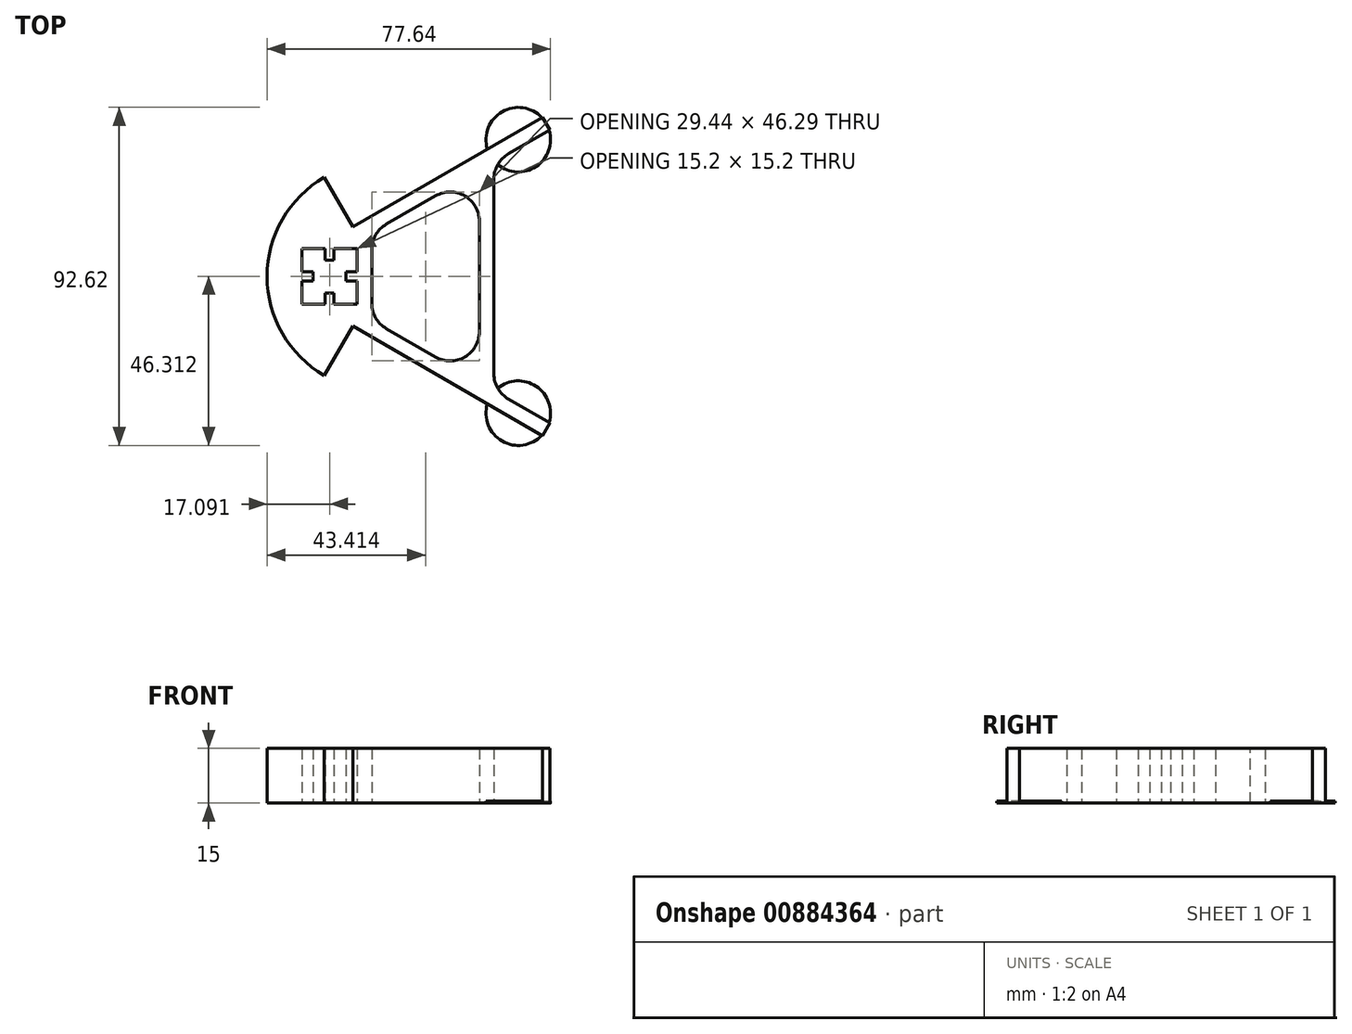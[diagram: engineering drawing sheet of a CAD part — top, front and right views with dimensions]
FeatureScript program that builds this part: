
annotation { "Feature Type Name" : "Feature", "Feature Type Description" : "" }
export const myFeature = defineFeature(function(context is Context, id is Id, definition is map)
    precondition{}
    {
        {
            var Q0;
            Q0=qCreatedBy(makeId("Top.planeOp"),FACE);
            var sketch = newSketch(context, id + "F0", { "sketchPlane" : qUnion([Q0])});
            skLineSegment(sketch, "E0.bottom", {"start": v(-11.65, 7.67) * mm, "end": v(-26.85, 7.67) * mm});
            skLineSegment(sketch, "E0.top", {"start": v(-11.65, -7.53) * mm, "end": v(-26.85, -7.53) * mm});
            skLineSegment(sketch, "E0.left", {"start": v(-11.65, 7.67) * mm, "end": v(-11.65, -7.53) * mm});
            skLineSegment(sketch, "E0.right", {"start": v(-26.85, 7.67) * mm, "end": v(-26.85, -7.53) * mm});
            skPoint(sketch, "E0.middle", {"position": v(-19.25, 0.07) * mm});
            skLineSegment(sketch, "E1", {"start": v(-7.65, 12.07) * mm, "end": v(-7.65, -11.93) * mm});
            skLineSegment(sketch, "E2", {"start": v(21.8, 29.07) * mm, "end": v(21.8, -28.93) * mm});
            skLineSegment(sketch, "E3", {"start": v(-7.65, 12.07) * mm, "end": v(21.8, 29.07) * mm});
            skLineSegment(sketch, "E4", {"start": v(-7.65, -11.93) * mm, "end": v(21.8, -28.93) * mm});
            skLineSegment(sketch, "E5", {"start": v(-12.84, 13.7) * mm, "end": v(39.12, 43.7) * mm});
            skLineSegment(sketch, "E6", {"start": v(-12.84, -13.55) * mm, "end": v(39.12, -43.55) * mm});
            skLineSegment(sketch, "E7", {"start": v(39.12, 43.7) * mm, "end": v(41.12, 40.23) * mm});
            skLineSegment(sketch, "E8", {"start": v(41.12, 40.23) * mm, "end": v(25.8, 31.38) * mm});
            skLineSegment(sketch, "E9", {"start": v(25.8, 31.38) * mm, "end": v(25.8, -31.24) * mm});
            skLineSegment(sketch, "E10", {"start": v(25.8, -31.24) * mm, "end": v(41.12, -40.08) * mm});
            skLineSegment(sketch, "E11", {"start": v(41.12, -40.08) * mm, "end": v(39.12, -43.55) * mm});
            skLineSegment(sketch, "E12", {"start": v(21.8, 29.07) * mm, "end": v(25.8, 31.38) * mm, "construction": true});
            skPoint(sketch, "E13", {"position": v(23.8, 30.23) * mm});
            skLineSegment(sketch, "E14", {"start": v(23.8, 30.23) * mm, "end": v(21.8, 33.7) * mm, "construction": true});
            skPoint(sketch, "E15", {"position": v(21.8, -33.55) * mm});
            skLineSegment(sketch, "E16", {"start": v(21.8, -28.93) * mm, "end": v(25.8, -31.24) * mm, "construction": true});
            skLineSegment(sketch, "E17", {"start": v(21.8, -33.55) * mm, "end": v(23.8, -30.08) * mm, "construction": true});
            skLineSegment(sketch, "E18", {"start": v(-12.84, 13.7) * mm, "end": v(-20.66, 27.23) * mm});
            skLineSegment(sketch, "E19", {"start": v(-12.84, -13.55) * mm, "end": v(-20.66, -27.08) * mm});
            skLineSegment(sketch, "E20", {"start": v(-12.84, -13.55) * mm, "end": v(-4.98, 0.07) * mm, "construction": true});
            skLineSegment(sketch, "E21", {"start": v(-12.84, 13.7) * mm, "end": v(-4.98, 0.07) * mm, "construction": true});
            skLineSegment(sketch, "E22", {"start": v(-11.65, 0.07) * mm, "end": v(-7.65, 0.07) * mm, "construction": true});
            skArc(sketch, "E23", {"start": v(-20.66, -27.08) * mm, "mid": v(-36.34, 0.07) * mm, "end": v(-20.66, 27.23) * mm});
            skLineSegment(sketch, "E24", {"start": v(-26.85, 1.32) * mm, "end": v(-23.75, 1.32) * mm});
            skLineSegment(sketch, "E25", {"start": v(-23.75, 1.32) * mm, "end": v(-23.75, -1.18) * mm});
            skLineSegment(sketch, "E26", {"start": v(-23.75, -1.18) * mm, "end": v(-26.85, -1.18) * mm});
            skLineSegment(sketch, "E27", {"start": v(-23.75, 0.07) * mm, "end": v(-26.85, 0.07) * mm, "construction": true});
            skLineSegment(sketch, "E28", {"start": v(-11.65, 1.32) * mm, "end": v(-14.75, 1.32) * mm});
            skLineSegment(sketch, "E29", {"start": v(-14.75, 1.32) * mm, "end": v(-14.75, -1.18) * mm});
            skLineSegment(sketch, "E30", {"start": v(-14.75, -1.18) * mm, "end": v(-11.65, -1.18) * mm});
            skLineSegment(sketch, "E31", {"start": v(-14.75, 0.07) * mm, "end": v(-11.65, 0.07) * mm, "construction": true});
            skLineSegment(sketch, "E32", {"start": v(-20.5, 7.67) * mm, "end": v(-20.5, 4.57) * mm});
            skLineSegment(sketch, "E33", {"start": v(-20.5, 4.57) * mm, "end": v(-18, 4.57) * mm});
            skLineSegment(sketch, "E34", {"start": v(-18, 4.57) * mm, "end": v(-18, 7.67) * mm});
            skLineSegment(sketch, "E35", {"start": v(-20.5, -7.53) * mm, "end": v(-20.5, -4.43) * mm});
            skLineSegment(sketch, "E36", {"start": v(-20.5, -4.43) * mm, "end": v(-18, -4.43) * mm});
            skLineSegment(sketch, "E37", {"start": v(-18, -4.43) * mm, "end": v(-18, -7.53) * mm});
            skLineSegment(sketch, "E38", {"start": v(-19.25, 4.57) * mm, "end": v(-19.25, 7.67) * mm, "construction": true});
            skLineSegment(sketch, "E39", {"start": v(-19.25, -4.43) * mm, "end": v(-19.25, -7.53) * mm, "construction": true});
            skLineSegment(sketch, "E40", {"start": v(39.12, 43.7) * mm, "end": v(25.8, 31.38) * mm, "construction": true});
            skLineSegment(sketch, "E41", {"start": v(39.12, -43.55) * mm, "end": v(25.8, -31.24) * mm, "construction": true});
            skCircle(sketch, "E42", {"center": v(32.46, 37.54) * mm, "radius": 8.85 * mm});
            skCircle(sketch, "E43", {"center": v(32.46, -37.4) * mm, "radius": 8.85 * mm});
            skSolve(sketch);
        }
        {
            var Q0;
            {var subQ0=sQuery(id+"F0.wireOp",EDGE,"E7");var subQ1=sQuery(id+"F0.wireOp",EDGE,"E5");var subQ2=makeQuery(id+"F0.imprint","INTERSECT",VERTEX,{"derivedFrom":[subQ1,subQ0]});Q0=makeQuery(id+"F0.imprint","IMPRINT",FACE,{"disambiguationData":[TD([[makeQuery(id+"F0.imprint","IMPRINT",EDGE,{"disambiguationData":[TD([[subQ2,1.0]])],"derivedFrom":subQ1}),-1.0]])]});}
            var Q1;
            {var subQ0=sQuery(id+"F0.wireOp",EDGE,"E11");var subQ1=sQuery(id+"F0.wireOp",EDGE,"E6");var subQ2=makeQuery(id+"F0.imprint","INTERSECT",VERTEX,{"derivedFrom":[subQ1,subQ0]});Q1=makeQuery(id+"F0.imprint","IMPRINT",FACE,{"disambiguationData":[TD([[makeQuery(id+"F0.imprint","IMPRINT",EDGE,{"disambiguationData":[TD([[subQ2,1.0]])],"derivedFrom":subQ1}),1.0]])]});}
            var Q2;
            {var subQ0=sQuery(id+"F0.wireOp",EDGE,"E8");var subQ1=sQuery(id+"F0.wireOp",EDGE,"E7");var subQ2=makeQuery(id+"F0.imprint","INTERSECT",VERTEX,{"derivedFrom":[subQ1,subQ0]});Q2=makeQuery(id+"F0.imprint","IMPRINT",FACE,{"disambiguationData":[TD([[makeQuery(id+"F0.imprint","IMPRINT",EDGE,{"disambiguationData":[TD([[subQ2,1.0]])],"derivedFrom":subQ1}),-1.0]])]});}
            var Q3;
            {var subQ0=sQuery(id+"F0.wireOp",EDGE,"E11");var subQ1=sQuery(id+"F0.wireOp",EDGE,"E10");var subQ2=makeQuery(id+"F0.imprint","INTERSECT",VERTEX,{"derivedFrom":[subQ1,subQ0]});Q3=makeQuery(id+"F0.imprint","IMPRINT",FACE,{"disambiguationData":[TD([[makeQuery(id+"F0.imprint","IMPRINT",EDGE,{"disambiguationData":[TD([[subQ2,1.0]])],"derivedFrom":subQ1}),-1.0]])]});}
            var Q4;
            {var subQ0=sQuery(id+"F0.wireOp",EDGE,"E42");var subQ1=sQuery(id+"F0.wireOp",EDGE,"E5");var subQ7=makeQuery(id+"F0.imprint","INTERSECT",VERTEX,{"disambiguationData":[OD(0.0)],"derivedFrom":[subQ1,subQ0]});Q4=makeQuery(id+"F0.imprint","IMPRINT",FACE,{"disambiguationData":[TD([[makeQuery(id+"F0.imprint","IMPRINT",EDGE,{"disambiguationData":[TD([[subQ7,-1.0]])],"derivedFrom":subQ1}),-1.0]])]});}
            var Q5;
            {var subQ0=sQuery(id+"F0.wireOp",EDGE,"E43");var subQ1=sQuery(id+"F0.wireOp",EDGE,"E6");var subQ2=makeQuery(id+"F0.imprint","INTERSECT",VERTEX,{"disambiguationData":[OD(0.0)],"derivedFrom":[subQ1,subQ0]});Q5=makeQuery(id+"F0.imprint","IMPRINT",FACE,{"disambiguationData":[TD([[makeQuery(id+"F0.imprint","IMPRINT",EDGE,{"disambiguationData":[TD([[subQ2,-1.0]])],"derivedFrom":subQ1}),1.0]])]});}
            var Q6;
            Q6=makeQuery(id+"F0.imprint","IMPRINT",FACE,{"disambiguationData":[TD([[makeQuery(id+"F0.imprint","IMPRINT",EDGE,{"derivedFrom":sQuery(id+"F0.wireOp",EDGE,"E1")}),-1.0]])]});
            var Q7;
            {var subQ0=sQuery(id+"F0.wireOp",EDGE,"E35");Q7=makeQuery(id+"F0.imprint","IMPRINT",FACE,{"disambiguationData":[TD([[makeQuery(id+"F0.imprint","IMPRINT",EDGE,{"derivedFrom":subQ0}),-1.0]])]});}
            var Q8;
            {var subQ0=sQuery(id+"F0.wireOp",EDGE,"E28");Q8=makeQuery(id+"F0.imprint","IMPRINT",FACE,{"disambiguationData":[TD([[makeQuery(id+"F0.imprint","IMPRINT",EDGE,{"derivedFrom":subQ0}),1.0]])]});}
            var Q9;
            {var subQ0=sQuery(id+"F0.wireOp",EDGE,"E32");Q9=makeQuery(id+"F0.imprint","IMPRINT",FACE,{"disambiguationData":[TD([[makeQuery(id+"F0.imprint","IMPRINT",EDGE,{"derivedFrom":subQ0}),1.0]])]});}
            var Q10;
            {var subQ0=sQuery(id+"F0.wireOp",EDGE,"E24");Q10=makeQuery(id+"F0.imprint","IMPRINT",FACE,{"disambiguationData":[TD([[makeQuery(id+"F0.imprint","IMPRINT",EDGE,{"derivedFrom":subQ0}),-1.0]])]});}
            extrude(context, id + "F1", {"entities" : qUnion([Q0, Q1, Q2, Q3, Q4, Q5, Q6, Q7, Q8, Q9, Q10]), "depth" : 15 * mm, "offsetDistance" : 25 * mm});
        }
        {
            var Q0;
            {var subQ0=sQuery(id+"F0.wireOp",EDGE,"E42");var subQ1=sQuery(id+"F0.wireOp",EDGE,"E5");var subQ2=makeQuery(id+"F0.imprint","INTERSECT",VERTEX,{"disambiguationData":[OD(0.0)],"derivedFrom":[subQ1,subQ0]});Q0=makeQuery(id+"F0.imprint","IMPRINT",FACE,{"disambiguationData":[TD([[makeQuery(id+"F0.imprint","IMPRINT",EDGE,{"disambiguationData":[TD([[subQ2,-1.0]])],"derivedFrom":subQ1}),1.0]])]});}
            var Q1;
            {var subQ0=sQuery(id+"F0.wireOp",EDGE,"E7");var subQ1=sQuery(id+"F0.wireOp",EDGE,"E5");var subQ2=makeQuery(id+"F0.imprint","INTERSECT",VERTEX,{"derivedFrom":[subQ1,subQ0]});Q1=makeQuery(id+"F0.imprint","IMPRINT",FACE,{"disambiguationData":[TD([[makeQuery(id+"F0.imprint","IMPRINT",EDGE,{"disambiguationData":[TD([[subQ2,1.0]])],"derivedFrom":subQ1}),-1.0]])]});}
            var Q2;
            {var subQ0=sQuery(id+"F0.wireOp",EDGE,"E43");var subQ1=sQuery(id+"F0.wireOp",EDGE,"E6");var subQ2=makeQuery(id+"F0.imprint","INTERSECT",VERTEX,{"disambiguationData":[OD(0.0)],"derivedFrom":[subQ1,subQ0]});Q2=makeQuery(id+"F0.imprint","IMPRINT",FACE,{"disambiguationData":[TD([[makeQuery(id+"F0.imprint","IMPRINT",EDGE,{"disambiguationData":[TD([[subQ2,-1.0]])],"derivedFrom":subQ1}),-1.0]])]});}
            var Q3;
            {var subQ0=sQuery(id+"F0.wireOp",EDGE,"E11");var subQ1=sQuery(id+"F0.wireOp",EDGE,"E6");var subQ2=makeQuery(id+"F0.imprint","INTERSECT",VERTEX,{"derivedFrom":[subQ1,subQ0]});Q3=makeQuery(id+"F0.imprint","IMPRINT",FACE,{"disambiguationData":[TD([[makeQuery(id+"F0.imprint","IMPRINT",EDGE,{"disambiguationData":[TD([[subQ2,1.0]])],"derivedFrom":subQ1}),1.0]])]});}
            var Q4;
            {var subQ0=sQuery(id+"F0.wireOp",EDGE,"E8");var subQ1=sQuery(id+"F0.wireOp",EDGE,"E7");var subQ2=makeQuery(id+"F0.imprint","INTERSECT",VERTEX,{"derivedFrom":[subQ1,subQ0]});Q4=makeQuery(id+"F0.imprint","IMPRINT",FACE,{"disambiguationData":[TD([[makeQuery(id+"F0.imprint","IMPRINT",EDGE,{"disambiguationData":[TD([[subQ2,1.0]])],"derivedFrom":subQ1}),-1.0]])]});}
            var Q5;
            {var subQ0=sQuery(id+"F0.wireOp",EDGE,"E42");var subQ1=sQuery(id+"F0.wireOp",EDGE,"E8");var subQ2=makeQuery(id+"F0.imprint","INTERSECT",VERTEX,{"disambiguationData":[OD(0.0)],"derivedFrom":[subQ1,subQ0]});Q5=makeQuery(id+"F0.imprint","IMPRINT",FACE,{"disambiguationData":[TD([[makeQuery(id+"F0.imprint","IMPRINT",EDGE,{"disambiguationData":[TD([[subQ2,-1.0]])],"derivedFrom":subQ1}),1.0]])]});}
            var Q6;
            {var subQ0=sQuery(id+"F0.wireOp",EDGE,"E43");var subQ1=sQuery(id+"F0.wireOp",EDGE,"E10");var subQ2=makeQuery(id+"F0.imprint","INTERSECT",VERTEX,{"disambiguationData":[OD(0.0)],"derivedFrom":[subQ1,subQ0]});Q6=makeQuery(id+"F0.imprint","IMPRINT",FACE,{"disambiguationData":[TD([[makeQuery(id+"F0.imprint","IMPRINT",EDGE,{"disambiguationData":[TD([[subQ2,-1.0]])],"derivedFrom":subQ1}),1.0]])]});}
            var Q7;
            {var subQ0=sQuery(id+"F0.wireOp",EDGE,"E11");var subQ1=sQuery(id+"F0.wireOp",EDGE,"E10");var subQ2=makeQuery(id+"F0.imprint","INTERSECT",VERTEX,{"derivedFrom":[subQ1,subQ0]});Q7=makeQuery(id+"F0.imprint","IMPRINT",FACE,{"disambiguationData":[TD([[makeQuery(id+"F0.imprint","IMPRINT",EDGE,{"disambiguationData":[TD([[subQ2,1.0]])],"derivedFrom":subQ1}),-1.0]])]});}
            extrude(context, id + "F2", {"entities" : qUnion([Q0, Q1, Q2, Q3, Q4, Q5, Q6, Q7]), "operationType" : NewBodyOperationType.ADD, "depth" : 0.6 * mm, "offsetDistance" : 25 * mm});
        }
        {
            var Q0;
            Q0=makeQuery(id+"F1.opExtrude","SWEPT_EDGE",EDGE,{"disambiguationData":[OSD([sQuery(id+"F0.wireOp",EDGE,"E1"),sQuery(id+"F0.wireOp",EDGE,"E3")])]});
            var Q1;
            Q1=makeQuery(id+"F1.opExtrude","SWEPT_EDGE",EDGE,{"disambiguationData":[OSD([sQuery(id+"F0.wireOp",EDGE,"E8"),sQuery(id+"F0.wireOp",EDGE,"E9")])]});
            var Q2;
            Q2=makeQuery(id+"F1.opExtrude","SWEPT_EDGE",EDGE,{"disambiguationData":[OSD([sQuery(id+"F0.wireOp",EDGE,"E2"),sQuery(id+"F0.wireOp",EDGE,"E3")])]});
            var Q3;
            Q3=makeQuery(id+"F1.opExtrude","SWEPT_EDGE",EDGE,{"disambiguationData":[OSD([sQuery(id+"F0.wireOp",EDGE,"E2"),sQuery(id+"F0.wireOp",EDGE,"E4")])]});
            var Q4;
            Q4=makeQuery(id+"F1.opExtrude","SWEPT_EDGE",EDGE,{"disambiguationData":[OSD([sQuery(id+"F0.wireOp",EDGE,"E9"),sQuery(id+"F0.wireOp",EDGE,"E10")])]});
            var Q5;
            Q5=makeQuery(id+"F1.opExtrude","SWEPT_EDGE",EDGE,{"disambiguationData":[OSD([sQuery(id+"F0.wireOp",EDGE,"E1"),sQuery(id+"F0.wireOp",EDGE,"E4")])]});
            fillet(context, id + "F3", {"entities" : qUnion([Q0, Q1, Q2, Q3, Q4, Q5]), "radius" : 8 * mm, "tangentPropagation" : true, "allowEdgeOverflow" : false});
        }
    });
